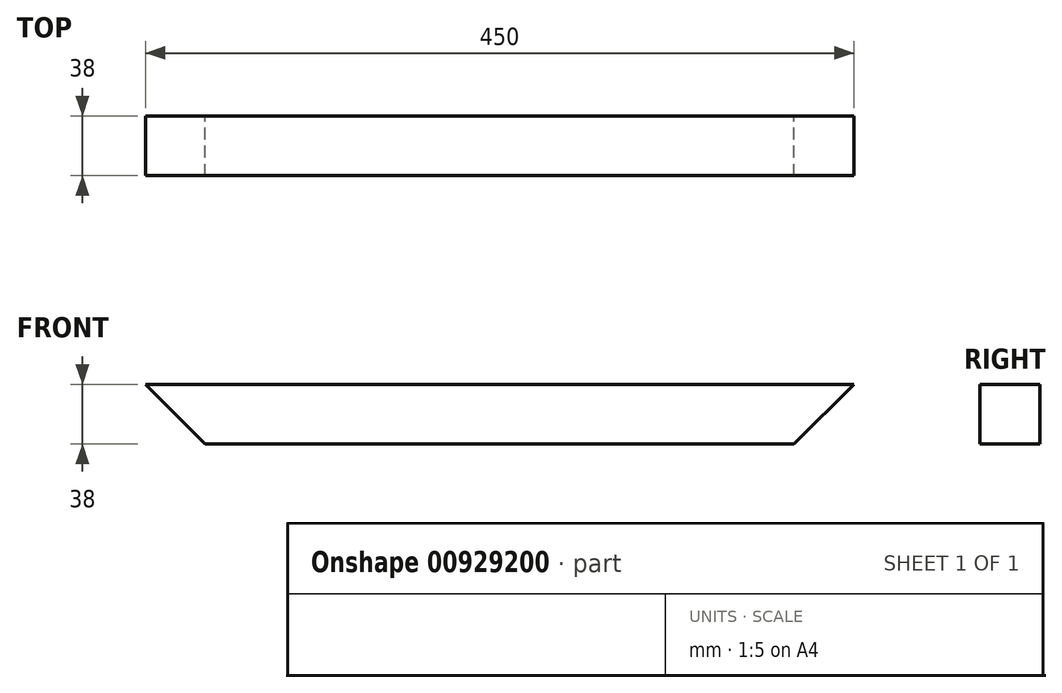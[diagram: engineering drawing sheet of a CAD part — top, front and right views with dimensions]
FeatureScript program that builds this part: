
annotation { "Feature Type Name" : "Feature", "Feature Type Description" : "" }
export const myFeature = defineFeature(function(context is Context, id is Id, definition is map)
    precondition{}
    {
        {
            var Q0;
            Q0=qCreatedBy(makeId("Front.planeOp"),FACE);
            var sketch = newSketch(context, id + "F0", { "sketchPlane" : qUnion([Q0])});
            skLineSegment(sketch, "E0", {"start": v(-169.53, 0) * mm, "end": v(280.47, 0) * mm});
            skLineSegment(sketch, "E1", {"start": v(280.47, 0) * mm, "end": v(242.47, -38) * mm});
            skLineSegment(sketch, "E2", {"start": v(242.47, -38) * mm, "end": v(-131.53, -38) * mm});
            skLineSegment(sketch, "E3", {"start": v(-131.53, -38) * mm, "end": v(-169.53, 0) * mm});
            skSolve(sketch);
        }
        {
            var Q0;
            Q0=qSketchRegion(id+"F0",true);
            extrude(context, id + "F1", {"entities" : qUnion([Q0]), "depth" : 38 * mm, "offsetDistance" : 25 * mm});
        }
        {
            var Q0;
            Q0=qCreatedBy(makeId("Front.planeOp"),FACE);
            var sketch = newSketch(context, id + "F2", { "sketchPlane" : qUnion([Q0])});
            skLineSegment(sketch, "E4", {"start": v(-285.73, 119.66) * mm, "end": v(-285.73, -254.34) * mm});
            skLineSegment(sketch, "E5", {"start": v(-285.73, -254.34) * mm, "end": v(-247.73, -254.34) * mm});
            skLineSegment(sketch, "E6", {"start": v(-247.73, -254.34) * mm, "end": v(-247.73, 119.66) * mm});
            skLineSegment(sketch, "E7", {"start": v(-247.73, 119.66) * mm, "end": v(-285.73, 119.66) * mm});
            skSolve(sketch);
        }
        {
            var Q0;
            Q0 = qSketchRegion(id + "F2", true);
            extrude(context, id + "F3", {"entities" : qUnion([Q0]), "depth" : 38 * mm, "offsetDistance" : 25 * mm});
        }
        {
            var Q0;
            Q0=makeQuery(id+"F3.opExtrude","SWEPT_BODY",BODY,{"disambiguationData":[OSD([sQuery(id+"F2.wireOp",EDGE,"E4"),sQuery(id+"F2.wireOp",EDGE,"E5"),sQuery(id+"F2.wireOp",EDGE,"E6"),sQuery(id+"F2.wireOp",EDGE,"E7")])]});
            deleteBodies(context, id + "F4", {"entities" : qUnion([Q0])});
        }
    });
